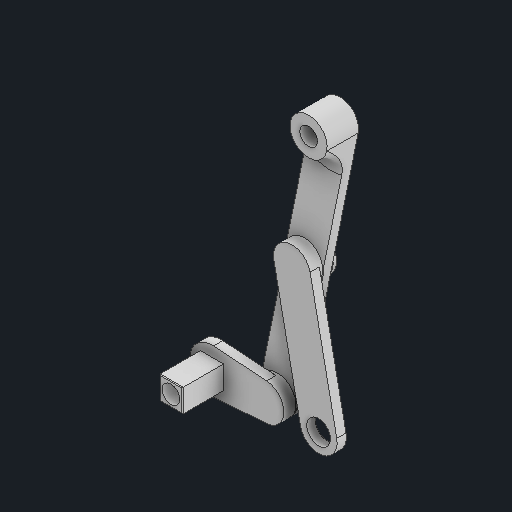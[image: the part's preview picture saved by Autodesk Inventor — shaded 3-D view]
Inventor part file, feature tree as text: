
AUTODESK INVENTOR PART (.ipt)
format: ipt  version: 2024.1 (Build 281209000, 209)  size: 195,584 bytes
history: native  units: in
note: dims shown in document units (in); Inventor stores cm internally (conversion verified against a paired STEP export)
features: sketch x5, other x3
ambient origin geometry x8: Origin, YZ Plane, XZ Plane, XY Plane, X Axis, Y Axis, Z Axis, Center Point
bodies: Solid1 (feature_tree)
feature tree (8):
  other  "FrontLinkage.ipt"
  other  "Solid1::FrontLinkage.ipt"
  other  "TaggingFeature1"
  sketch  "Sketch1"  dims[d0=0.3937in]
  sketch  "Sketch2"
  sketch  "Sketch3"
  sketch  "Sketch4"
  sketch  "Sketch5"
